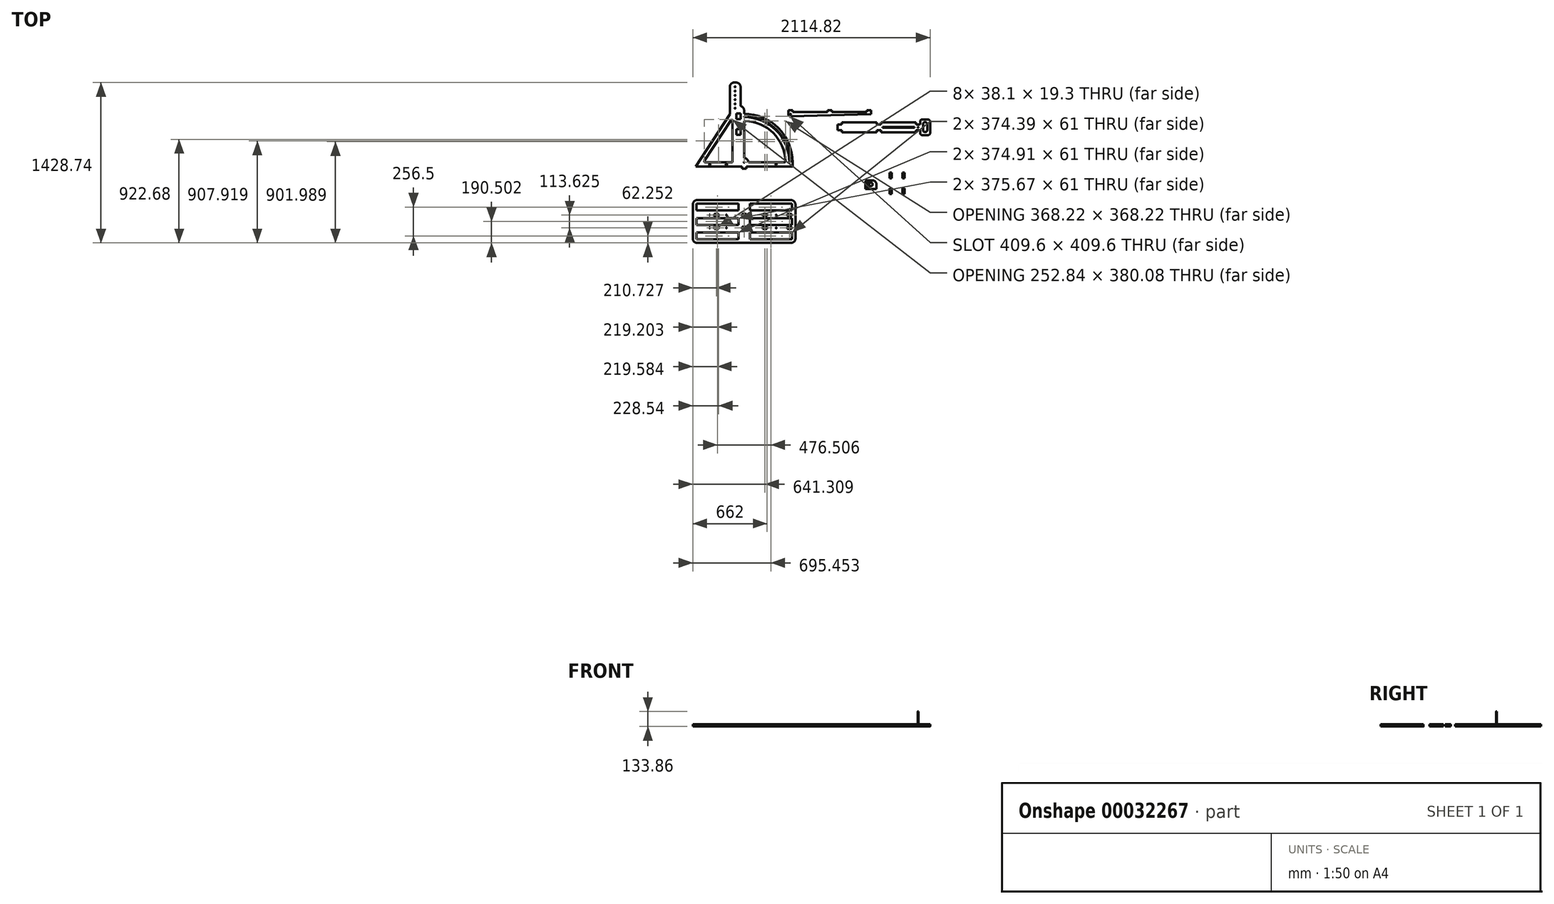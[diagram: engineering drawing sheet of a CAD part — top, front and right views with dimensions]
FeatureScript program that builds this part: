
annotation { "Feature Type Name" : "Feature", "Feature Type Description" : "" }
export const myFeature = defineFeature(function(context is Context, id is Id, definition is map)
    precondition{}
    {
        {
            var Q0;
            Q0=qCreatedBy(makeId("Top.planeOp"),FACE);
            var sketch = newSketch(context, id + "F0", { "sketchPlane" : qUnion([Q0])});
            skLineSegment(sketch, "E0", {"start": v(-431.8, -38.1) * mm, "end": v(431.8, -38.1) * mm});
            skLineSegment(sketch, "E1", {"start": v(0, -38.1) * mm, "end": v(0, 368.3) * mm});
            skPoint(sketch, "E1.startSnap0", {"position": v(0, -38.1) * mm});
            skLineSegment(sketch, "E2", {"start": v(-127, 429.94) * mm, "end": v(-431.8, -38.1) * mm});
            skLineSegment(sketch, "E3", {"start": v(-127, 711.32) * mm, "end": v(-31.75, 710.17) * mm});
            skLineSegment(sketch, "E4", {"start": v(-127, 711.32) * mm, "end": v(-127, 429.94) * mm});
            skLineSegment(sketch, "E5", {"start": v(431.8, -38.1) * mm, "end": v(431.8, 0) * mm});
            skLineSegment(sketch, "E6", {"start": v(409.6, 0) * mm, "end": v(403.2, 0) * mm});
            skArc(sketch, "E7", {"start": v(38.1, 0) * mm, "mid": v(26.94, 26.94) * mm, "end": v(0, 38.1) * mm});
            skLineSegment(sketch, "E8", {"start": v(1130.5, 427.69) * mm, "end": v(1130.5, 446.74) * mm});
            skLineSegment(sketch, "E9", {"start": v(413.41, 409.73) * mm, "end": v(1130.5, 427.69) * mm});
            skPoint(sketch, "E10", {"position": v(412.93, 428.78) * mm});
            skCircle(sketch, "E11", {"center": v(412.93, 428.78) * mm, "radius": 3.37 * mm});
            skArc(sketch, "E12", {"start": v(431.8, 0) * mm, "mid": v(305.33, 305.33) * mm, "end": v(0, 431.8) * mm});
            skArc(sketch, "E13", {"start": v(368.3, 0) * mm, "mid": v(260.43, 260.43) * mm, "end": v(0, 368.3) * mm});
            skArc(sketch, "E14.trimOffspring", {"start": v(403.2, 0) * mm, "mid": v(285.1, 285.1) * mm, "end": v(0, 403.2) * mm});
            skArc(sketch, "E15.trimOffspring", {"start": v(409.6, 0) * mm, "mid": v(289.63, 289.63) * mm, "end": v(0, 409.6) * mm});
            skLineSegment(sketch, "E16", {"start": v(-102.24, 0) * mm, "end": v(-361.52, 0) * mm});
            skLineSegment(sketch, "E17", {"start": v(-361.52, 0) * mm, "end": v(-102.24, 398.13) * mm});
            skLineSegment(sketch, "E18", {"start": v(-102.24, 398.13) * mm, "end": v(-102.24, 0) * mm});
            skLineSegment(sketch, "E19.trimOffspring", {"start": v(368.3, 0) * mm, "end": v(0, 0) * mm});
            skLineSegment(sketch, "E20.trimOffspring", {"start": v(0, 431.8) * mm, "end": v(0, 501.49) * mm});
            skLineSegment(sketch, "E21.trimOffspring", {"start": v(0, 403.2) * mm, "end": v(0, 409.6) * mm});
            skLineSegment(sketch, "E22.rect.bottom", {"start": v(19.05, -38.1) * mm, "end": v(-19.05, -38.1) * mm});
            skLineSegment(sketch, "E22.rect.top", {"start": v(19.05, -56.13) * mm, "end": v(-19.05, -56.13) * mm});
            skLineSegment(sketch, "E22.rect.left", {"start": v(19.05, -38.1) * mm, "end": v(19.05, -56.13) * mm});
            skLineSegment(sketch, "E22.rect.right", {"start": v(-19.05, -38.1) * mm, "end": v(-19.05, -56.13) * mm});
            skLineSegment(sketch, "E23.rect.bottom", {"start": v(-227.42, -38.1) * mm, "end": v(-265.52, -38.1) * mm});
            skLineSegment(sketch, "E23.rect.left", {"start": v(-227.42, -38.1) * mm, "end": v(-227.42, -56.13) * mm});
            skLineSegment(sketch, "E23.rect.top", {"start": v(-227.42, -56.13) * mm, "end": v(-265.52, -56.13) * mm});
            skLineSegment(sketch, "E23.rect.right", {"start": v(-265.52, -38.1) * mm, "end": v(-265.52, -56.13) * mm});
            skLineSegment(sketch, "E24.rect.bottom", {"start": v(422.25, -38.1) * mm, "end": v(384.15, -38.1) * mm});
            skLineSegment(sketch, "E24.rect.left", {"start": v(422.25, -38.1) * mm, "end": v(422.25, -56.13) * mm});
            skLineSegment(sketch, "E24.rect.top", {"start": v(422.25, -56.13) * mm, "end": v(384.15, -56.13) * mm});
            skLineSegment(sketch, "E24.rect.right", {"start": v(384.15, -38.1) * mm, "end": v(384.15, -56.13) * mm});
            skLineSegment(sketch, "E25.rect.bottom", {"start": v(203.2, -38.1) * mm, "end": v(165.1, -38.1) * mm});
            skLineSegment(sketch, "E25.rect.left", {"start": v(203.2, -38.1) * mm, "end": v(203.2, -56.13) * mm});
            skLineSegment(sketch, "E25.rect.top", {"start": v(203.2, -56.13) * mm, "end": v(165.1, -56.13) * mm});
            skLineSegment(sketch, "E25.rect.right", {"start": v(165.1, -38.1) * mm, "end": v(165.1, -56.13) * mm});
            skPoint(sketch, "E26", {"position": v(285.75, -19.05) * mm});
            skCircle(sketch, "E27", {"center": v(-306.23, -19.05) * mm, "radius": 5.33 * mm});
            skCircle(sketch, "E28", {"center": v(-157.54, -19.05) * mm, "radius": 5.33 * mm});
            skCircle(sketch, "E29", {"center": v(285.75, -19.05) * mm, "radius": 5.33 * mm});
            skLineSegment(sketch, "E30", {"start": v(-31.75, 571.18) * mm, "end": v(-31.75, 501.49) * mm});
            skLineSegment(sketch, "E31", {"start": v(-31.75, 501.49) * mm, "end": v(0, 501.49) * mm});
            skLineSegment(sketch, "E32", {"start": v(-31.75, 501.49) * mm, "end": v(-31.75, 710.17) * mm});
            skLineSegment(sketch, "E33", {"start": v(-79.37, 710.75) * mm, "end": v(-79.83, 672.65) * mm});
            skCircle(sketch, "E34", {"center": v(-79.83, 672.65) * mm, "radius": 3.3 * mm});
            skLineSegment(sketch, "E35", {"start": v(-79.83, 672.65) * mm, "end": v(-79.83, 634.55) * mm});
            skCircle(sketch, "E36.0.1.0", {"center": v(-79.83, 634.55) * mm, "radius": 3.3 * mm});
            skCircle(sketch, "E36.0.2.0", {"center": v(-79.83, 596.45) * mm, "radius": 3.3 * mm});
            skCircle(sketch, "E36.0.3.0", {"center": v(-79.83, 558.35) * mm, "radius": 3.3 * mm});
            skLineSegment(sketch, "E36.direction1", {"start": v(-79.83, 672.65) * mm, "end": v(-54.43, 672.65) * mm, "construction": true});
            skLineSegment(sketch, "E36.direction2", {"start": v(-79.83, 672.65) * mm, "end": v(-79.83, 634.55) * mm, "construction": true});
            skCircle(sketch, "E37", {"center": v(0, 0) * mm, "radius": 3.3 * mm});
            skLineSegment(sketch, "E38", {"start": v(393.9, 427.69) * mm, "end": v(393.9, 446.74) * mm});
            skArc(sketch, "E39.trimOffspring", {"start": v(393.9, 427.69) * mm, "mid": v(400.02, 414.76) * mm, "end": v(413.41, 409.73) * mm});
            skLineSegment(sketch, "E40.bottom", {"start": v(832.12, 356.64) * mm, "end": v(1568.72, 356.64) * mm});
            skLineSegment(sketch, "E40.top", {"start": v(832.12, 267.74) * mm, "end": v(1568.72, 267.74) * mm});
            skLineSegment(sketch, "E40.left", {"start": v(832.12, 356.64) * mm, "end": v(832.12, 267.74) * mm});
            skLineSegment(sketch, "E41.bottom", {"start": v(1568.72, 382.04) * mm, "end": v(1657.62, 382.04) * mm});
            skLineSegment(sketch, "E41.top", {"start": v(1568.72, 242.34) * mm, "end": v(1657.62, 242.34) * mm});
            skLineSegment(sketch, "E41.left", {"start": v(1568.72, 382.04) * mm, "end": v(1568.72, 356.64) * mm});
            skLineSegment(sketch, "E41.right", {"start": v(1657.62, 382.04) * mm, "end": v(1657.62, 242.34) * mm});
            skPoint(sketch, "E42", {"position": v(1568.72, 312.19) * mm});
            skLineSegment(sketch, "E43.bottom", {"start": v(1594.12, 357.9) * mm, "end": v(1632.22, 357.9) * mm});
            skLineSegment(sketch, "E43.top", {"start": v(1594.12, 269) * mm, "end": v(1632.22, 269) * mm});
            skLineSegment(sketch, "E43.left", {"start": v(1594.12, 357.9) * mm, "end": v(1594.12, 269) * mm});
            skLineSegment(sketch, "E43.right", {"start": v(1632.22, 357.9) * mm, "end": v(1632.22, 269) * mm});
            skPoint(sketch, "E44", {"position": v(1621.35, 313.44) * mm});
            skLineSegment(sketch, "E45.trimOffspring", {"start": v(1568.72, 267.74) * mm, "end": v(1568.72, 242.34) * mm});
            skLineSegment(sketch, "E46.rect.bottom", {"start": v(432, 464.77) * mm, "end": v(393.9, 464.77) * mm});
            skLineSegment(sketch, "E46.rect.left", {"start": v(432, 464.77) * mm, "end": v(432, 446.74) * mm});
            skLineSegment(sketch, "E46.rect.right", {"start": v(393.9, 464.77) * mm, "end": v(393.9, 446.74) * mm});
            skLineSegment(sketch, "E47.rect.bottom", {"start": v(1130.5, 464.77) * mm, "end": v(1092.4, 464.77) * mm});
            skLineSegment(sketch, "E47.rect.left", {"start": v(1130.5, 464.77) * mm, "end": v(1130.5, 446.74) * mm});
            skLineSegment(sketch, "E47.rect.top", {"start": v(1130.5, 446.74) * mm, "end": v(1092.4, 446.74) * mm});
            skLineSegment(sketch, "E47.rect.right", {"start": v(1092.4, 464.77) * mm, "end": v(1092.4, 446.74) * mm});
            skLineSegment(sketch, "E48.rect.bottom", {"start": v(781.26, 464.77) * mm, "end": v(743.16, 464.77) * mm});
            skLineSegment(sketch, "E48.rect.left", {"start": v(781.26, 464.77) * mm, "end": v(781.26, 446.74) * mm});
            skLineSegment(sketch, "E48.rect.top", {"start": v(781.26, 446.74) * mm, "end": v(743.16, 446.74) * mm});
            skLineSegment(sketch, "E48.rect.right", {"start": v(743.16, 464.77) * mm, "end": v(743.16, 446.74) * mm});
            skPoint(sketch, "E49", {"position": v(762.2, 446.74) * mm});
            skLineSegment(sketch, "E50", {"start": v(393.9, 446.74) * mm, "end": v(1130.5, 446.74) * mm});
            skLineSegment(sketch, "E51.rect.top", {"start": v(870.22, 267.74) * mm, "end": v(832.12, 267.74) * mm});
            skLineSegment(sketch, "E51.rect.left", {"start": v(870.22, 287.04) * mm, "end": v(870.22, 267.74) * mm});
            skLineSegment(sketch, "E51.rect.bottom", {"start": v(870.22, 287.04) * mm, "end": v(832.12, 287.04) * mm});
            skLineSegment(sketch, "E52", {"start": v(832.12, 287.04) * mm, "end": v(832.12, 267.74) * mm});
            skLineSegment(sketch, "E53.rect.top", {"start": v(870.22, 337.34) * mm, "end": v(832.12, 337.34) * mm});
            skLineSegment(sketch, "E53.rect.left", {"start": v(870.22, 356.64) * mm, "end": v(870.22, 337.34) * mm});
            skLineSegment(sketch, "E53.rect.bottom", {"start": v(870.22, 356.64) * mm, "end": v(832.12, 356.64) * mm});
            skLineSegment(sketch, "E54.rect.top", {"start": v(1219.47, 337.34) * mm, "end": v(1181.37, 337.34) * mm});
            skLineSegment(sketch, "E54.rect.left", {"start": v(1219.47, 356.64) * mm, "end": v(1219.47, 337.34) * mm});
            skLineSegment(sketch, "E54.rect.bottom", {"start": v(1219.47, 356.64) * mm, "end": v(1181.37, 356.64) * mm});
            skLineSegment(sketch, "E54.rect.right", {"start": v(1181.37, 356.64) * mm, "end": v(1181.37, 337.34) * mm});
            skLineSegment(sketch, "E55.rect.top", {"start": v(1568.72, 337.34) * mm, "end": v(1530.62, 337.34) * mm});
            skLineSegment(sketch, "E55.rect.left", {"start": v(1568.72, 356.64) * mm, "end": v(1568.72, 337.34) * mm});
            skLineSegment(sketch, "E55.rect.bottom", {"start": v(1568.72, 356.64) * mm, "end": v(1530.62, 356.64) * mm});
            skLineSegment(sketch, "E55.rect.right", {"start": v(1530.62, 356.64) * mm, "end": v(1530.62, 337.34) * mm});
            skLineSegment(sketch, "E56", {"start": v(832.12, 356.64) * mm, "end": v(832.12, 337.34) * mm});
            skPoint(sketch, "E57", {"position": v(1200.42, 356.64) * mm});
            skLineSegment(sketch, "E58.rect.right", {"start": v(1181.37, 287.04) * mm, "end": v(1181.37, 267.74) * mm});
            skLineSegment(sketch, "E58.rect.left", {"start": v(1219.47, 287.04) * mm, "end": v(1219.47, 267.74) * mm});
            skLineSegment(sketch, "E58.rect.top", {"start": v(1219.47, 267.74) * mm, "end": v(1181.37, 267.74) * mm});
            skLineSegment(sketch, "E58.rect.bottom", {"start": v(1219.47, 287.04) * mm, "end": v(1181.37, 287.04) * mm});
            skLineSegment(sketch, "E59.rect.bottom", {"start": v(1568.72, 287.04) * mm, "end": v(1530.62, 287.04) * mm});
            skLineSegment(sketch, "E59.rect.left", {"start": v(1568.72, 287.04) * mm, "end": v(1568.72, 267.74) * mm});
            skLineSegment(sketch, "E59.rect.right", {"start": v(1530.62, 287.04) * mm, "end": v(1530.62, 267.74) * mm});
            skLineSegment(sketch, "E59.rect.top", {"start": v(1568.72, 267.74) * mm, "end": v(1530.62, 267.74) * mm});
            skPoint(sketch, "E60", {"position": v(1613.17, 357.9) * mm});
            skPoint(sketch, "E61", {"position": v(1200.42, 267.74) * mm});
            skLineSegment(sketch, "E62.bottom", {"start": v(-457.2, -336.88) * mm, "end": v(457.2, -336.88) * mm});
            skLineSegment(sketch, "E62.top", {"start": v(-457.2, -717.88) * mm, "end": v(457.2, -717.88) * mm});
            skLineSegment(sketch, "E62.left", {"start": v(-457.2, -336.88) * mm, "end": v(-457.2, -717.88) * mm});
            skLineSegment(sketch, "E62.right", {"start": v(457.2, -336.88) * mm, "end": v(457.2, -717.88) * mm});
            skLineSegment(sketch, "E63.left", {"start": v(-457.2, -479.75) * mm, "end": v(-457.2, -575) * mm});
            skLineSegment(sketch, "E63.right", {"start": v(457.2, -479.75) * mm, "end": v(457.2, -575) * mm});
            skPoint(sketch, "E64", {"position": v(-457.2, -527.38) * mm});
            skLineSegment(sketch, "E65.rect.left", {"start": v(-227.42, -461.38) * mm, "end": v(-227.42, -480.68) * mm});
            skLineSegment(sketch, "E65.rect.top", {"start": v(-227.42, -480.68) * mm, "end": v(-265.52, -480.68) * mm});
            skLineSegment(sketch, "E66", {"start": v(-265.52, -461.38) * mm, "end": v(-265.52, -480.68) * mm});
            skLineSegment(sketch, "E65.rect.bottom", {"start": v(-227.42, -461.38) * mm, "end": v(-265.52, -461.38) * mm});
            skLineSegment(sketch, "E67.rect.left", {"start": v(19.05, -460.45) * mm, "end": v(19.05, -479.75) * mm});
            skLineSegment(sketch, "E67.rect.top", {"start": v(19.05, -479.75) * mm, "end": v(-19.05, -479.75) * mm});
            skLineSegment(sketch, "E68", {"start": v(-19.05, -460.45) * mm, "end": v(-19.05, -479.75) * mm});
            skLineSegment(sketch, "E67.rect.bottom", {"start": v(19.05, -460.45) * mm, "end": v(-19.05, -460.45) * mm});
            skLineSegment(sketch, "E69.rect.left", {"start": v(203.2, -460.45) * mm, "end": v(203.2, -479.75) * mm});
            skLineSegment(sketch, "E69.rect.top", {"start": v(203.2, -479.75) * mm, "end": v(165.1, -479.75) * mm});
            skLineSegment(sketch, "E70", {"start": v(165.1, -460.45) * mm, "end": v(165.1, -479.75) * mm});
            skLineSegment(sketch, "E69.rect.bottom", {"start": v(203.2, -460.45) * mm, "end": v(165.1, -460.45) * mm});
            skLineSegment(sketch, "E71.rect.left", {"start": v(422.25, -460.45) * mm, "end": v(422.25, -479.75) * mm});
            skLineSegment(sketch, "E71.rect.top", {"start": v(422.25, -479.75) * mm, "end": v(384.15, -479.75) * mm});
            skLineSegment(sketch, "E72", {"start": v(384.15, -460.45) * mm, "end": v(384.15, -479.75) * mm});
            skLineSegment(sketch, "E71.rect.bottom", {"start": v(422.25, -460.45) * mm, "end": v(384.15, -460.45) * mm});
            skLineSegment(sketch, "E73.rect.left", {"start": v(-227.42, -575) * mm, "end": v(-227.42, -594.3) * mm});
            skLineSegment(sketch, "E73.rect.top", {"start": v(-227.42, -594.3) * mm, "end": v(-265.52, -594.3) * mm});
            skLineSegment(sketch, "E74", {"start": v(-265.52, -575) * mm, "end": v(-265.52, -594.3) * mm});
            skLineSegment(sketch, "E73.rect.bottom", {"start": v(-227.42, -575) * mm, "end": v(-265.52, -575) * mm});
            skLineSegment(sketch, "E75.rect.left", {"start": v(19.05, -575) * mm, "end": v(19.05, -594.3) * mm});
            skLineSegment(sketch, "E75.rect.top", {"start": v(19.05, -594.3) * mm, "end": v(-19.05, -594.3) * mm});
            skLineSegment(sketch, "E76", {"start": v(-19.05, -575) * mm, "end": v(-19.05, -594.3) * mm});
            skLineSegment(sketch, "E75.rect.bottom", {"start": v(19.05, -575) * mm, "end": v(-19.05, -575) * mm});
            skLineSegment(sketch, "E77.rect.left", {"start": v(203.2, -575) * mm, "end": v(203.2, -594.3) * mm});
            skLineSegment(sketch, "E77.rect.top", {"start": v(203.2, -594.3) * mm, "end": v(165.1, -594.3) * mm});
            skLineSegment(sketch, "E78", {"start": v(165.1, -575) * mm, "end": v(165.1, -594.3) * mm});
            skLineSegment(sketch, "E77.rect.bottom", {"start": v(203.2, -575) * mm, "end": v(165.1, -575) * mm});
            skLineSegment(sketch, "E79.rect.left", {"start": v(422.25, -575) * mm, "end": v(422.25, -594.3) * mm});
            skLineSegment(sketch, "E79.rect.top", {"start": v(422.25, -594.3) * mm, "end": v(384.15, -594.3) * mm});
            skLineSegment(sketch, "E80", {"start": v(384.15, -575) * mm, "end": v(384.15, -594.3) * mm});
            skLineSegment(sketch, "E79.rect.bottom", {"start": v(422.25, -575) * mm, "end": v(384.15, -575) * mm});
            skLineSegment(sketch, "E81", {"start": v(-265.52, -38.1) * mm, "end": v(-265.52, -32.4) * mm, "construction": true});
            skPoint(sketch, "E82", {"position": v(-265.52, -38.1) * mm});
            skPoint(sketch, "E83.startSnap0", {"position": v(-265.52, -471.03) * mm});
            skPoint(sketch, "E83.endSnap0", {"position": v(203.2, -470.1) * mm});
            skPoint(sketch, "E84.endSnap0", {"position": v(203.2, -584.66) * mm});
            skCircle(sketch, "E85", {"center": v(-306.23, -470.12) * mm, "radius": 3.3 * mm});
            skCircle(sketch, "E86", {"center": v(-306.23, -584.66) * mm, "radius": 3.3 * mm});
            skCircle(sketch, "E87", {"center": v(-157.54, -470.1) * mm, "radius": 3.3 * mm});
            skCircle(sketch, "E88", {"center": v(-157.54, -584.66) * mm, "radius": 3.3 * mm});
            skCircle(sketch, "E89", {"center": v(285.75, -470.1) * mm, "radius": 3.3 * mm});
            skCircle(sketch, "E90", {"center": v(285.75, -584.66) * mm, "radius": 3.3 * mm});
            skCircle(sketch, "E91", {"center": v(1549.67, 312.19) * mm, "radius": 3.3 * mm});
            skLineSegment(sketch, "E92", {"start": v(-31.75, 436.83) * mm, "end": v(-31.75, 386.03) * mm});
            skLineSegment(sketch, "E93", {"start": v(-31.75, 386.03) * mm, "end": v(-69.34, 386.03) * mm});
            skLineSegment(sketch, "E94", {"start": v(-69.34, 386.03) * mm, "end": v(-69.34, 436.83) * mm});
            skLineSegment(sketch, "E95", {"start": v(-69.34, 436.83) * mm, "end": v(-31.75, 436.83) * mm});
            skLineSegment(sketch, "E96", {"start": v(-31.75, 297.13) * mm, "end": v(-31.75, 246.33) * mm});
            skLineSegment(sketch, "E97", {"start": v(-69.34, 246.33) * mm, "end": v(-69.34, 297.13) * mm});
            skLineSegment(sketch, "E98", {"start": v(-31.75, 246.33) * mm, "end": v(-69.34, 246.33) * mm});
            skLineSegment(sketch, "E99", {"start": v(-69.34, 297.13) * mm, "end": v(-31.75, 297.13) * mm});
            skLineSegment(sketch, "E100.bottom", {"start": v(1517.92, 315.5) * mm, "end": v(1232.17, 315.5) * mm});
            skLineSegment(sketch, "E100.top", {"start": v(1517.92, 308.89) * mm, "end": v(1232.17, 308.89) * mm});
            skLineSegment(sketch, "E100.left", {"start": v(1517.92, 315.5) * mm, "end": v(1517.92, 308.89) * mm});
            skLineSegment(sketch, "E100.right", {"start": v(1232.17, 315.5) * mm, "end": v(1232.17, 308.89) * mm});
            skLineSegment(sketch, "E101", {"start": v(1632.22, 312.19) * mm, "end": v(1517.92, 312.19) * mm, "construction": true});
            skPoint(sketch, "E101.startSnap0", {"position": v(1632.22, 313.44) * mm});
            skPoint(sketch, "E102", {"position": v(1517.92, 312.19) * mm});
            skLineSegment(sketch, "E103.bottom", {"start": v(1079.65, -160.08) * mm, "end": v(1179.88, -160.08) * mm});
            skLineSegment(sketch, "E103.top", {"start": v(1079.65, -236.28) * mm, "end": v(1179.88, -236.28) * mm});
            skLineSegment(sketch, "E103.left", {"start": v(1079.65, -160.08) * mm, "end": v(1079.65, -236.28) * mm});
            skLineSegment(sketch, "E103.right", {"start": v(1179.88, -160.08) * mm, "end": v(1179.88, -236.28) * mm});
            skArc(sketch, "E104", {"start": v(1115.7, -189.34) * mm, "mid": v(1138.42, -210) * mm, "end": v(1128.78, -180.84) * mm});
            skPoint(sketch, "E104.centerSnap0", {"position": v(1129.77, -236.28) * mm});
            skLineSegment(sketch, "E105", {"start": v(1079.65, -183.9) * mm, "end": v(1128.78, -180.84) * mm});
            skLineSegment(sketch, "E106", {"start": v(1115.7, -189.34) * mm, "end": v(1079.65, -191.59) * mm});
            skLineSegment(sketch, "E107.bottom", {"start": v(1297.48, -92.92) * mm, "end": v(1429.82, -92.92) * mm});
            skLineSegment(sketch, "E107.top", {"start": v(1297.48, -283.42) * mm, "end": v(1429.82, -283.42) * mm});
            skLineSegment(sketch, "E107.left", {"start": v(1297.48, -92.92) * mm, "end": v(1297.48, -143.72) * mm});
            skLineSegment(sketch, "E107.right", {"start": v(1429.82, -92.92) * mm, "end": v(1429.82, -143.72) * mm});
            skLineSegment(sketch, "E108", {"start": v(1297.48, -143.72) * mm, "end": v(1297.48, -92.92) * mm});
            skLineSegment(sketch, "E109", {"start": v(1297.48, -92.92) * mm, "end": v(1315.77, -92.92) * mm});
            skLineSegment(sketch, "E110", {"start": v(1315.77, -143.72) * mm, "end": v(1297.48, -143.72) * mm});
            skLineSegment(sketch, "E111", {"start": v(1315.77, -92.92) * mm, "end": v(1315.77, -143.72) * mm});
            skLineSegment(sketch, "E112", {"start": v(1411.53, -92.92) * mm, "end": v(1429.82, -92.92) * mm});
            skLineSegment(sketch, "E113", {"start": v(1411.53, -143.72) * mm, "end": v(1411.53, -92.92) * mm});
            skLineSegment(sketch, "E114", {"start": v(1429.82, -143.72) * mm, "end": v(1411.53, -143.72) * mm});
            skLineSegment(sketch, "E115", {"start": v(1411.53, -232.62) * mm, "end": v(1429.82, -232.62) * mm});
            skLineSegment(sketch, "E116", {"start": v(1411.53, -283.42) * mm, "end": v(1411.53, -232.62) * mm});
            skLineSegment(sketch, "E117", {"start": v(1429.82, -232.62) * mm, "end": v(1429.82, -283.42) * mm});
            skLineSegment(sketch, "E118", {"start": v(1429.82, -283.42) * mm, "end": v(1411.53, -283.42) * mm});
            skLineSegment(sketch, "E119", {"start": v(1297.48, -232.62) * mm, "end": v(1315.77, -232.62) * mm});
            skLineSegment(sketch, "E120", {"start": v(1297.48, -283.42) * mm, "end": v(1297.48, -232.62) * mm});
            skLineSegment(sketch, "E121", {"start": v(1315.77, -232.62) * mm, "end": v(1315.77, -283.42) * mm});
            skLineSegment(sketch, "E122", {"start": v(1315.77, -283.42) * mm, "end": v(1297.48, -283.42) * mm});
            skLineSegment(sketch, "E123", {"start": v(1315.77, -143.72) * mm, "end": v(1315.77, -232.62) * mm});
            skLineSegment(sketch, "E124", {"start": v(1411.53, -143.72) * mm, "end": v(1411.53, -232.62) * mm});
            skLineSegment(sketch, "E125.trimOffspring", {"start": v(1297.48, -232.62) * mm, "end": v(1297.48, -283.42) * mm});
            skCircle(sketch, "E126", {"center": v(1098.7, -217.23) * mm, "radius": 5.33 * mm});
            skPoint(sketch, "E127", {"position": v(1098.7, -211.9) * mm});
            skLineSegment(sketch, "E128", {"start": v(-50.54, -368.63) * mm, "end": v(-50.54, -429.63) * mm});
            skPoint(sketch, "E128.startSnap0", {"position": v(-50.54, 246.33) * mm});
            skPoint(sketch, "E129.endSnap0", {"position": v(0, -575) * mm});
            skLineSegment(sketch, "E130.MirrorCS", {"start": v(51.06, -368.63) * mm, "end": v(51.06, -429.63) * mm});
            skLineSegment(sketch, "E131.bottom", {"start": v(-50.54, -429.63) * mm, "end": v(-425.45, -429.63) * mm});
            skLineSegment(sketch, "E131.top", {"start": v(-50.54, -368.63) * mm, "end": v(-425.45, -368.63) * mm});
            skLineSegment(sketch, "E131.left", {"start": v(-50.54, -429.63) * mm, "end": v(-50.54, -368.63) * mm});
            skLineSegment(sketch, "E131.right", {"start": v(-425.45, -429.63) * mm, "end": v(-425.45, -368.63) * mm});
            skLineSegment(sketch, "E132.MirrorCS", {"start": v(-50.54, -686.13) * mm, "end": v(-426.21, -686.13) * mm});
            skLineSegment(sketch, "E133.MirrorCS", {"start": v(-50.54, -625.13) * mm, "end": v(-425.45, -625.13) * mm});
            skLineSegment(sketch, "E134.MirrorCS", {"start": v(-425.45, -625.13) * mm, "end": v(-425.45, -686.13) * mm});
            skLineSegment(sketch, "E135.MirrorCS", {"start": v(51.06, -368.63) * mm, "end": v(425.45, -368.63) * mm});
            skLineSegment(sketch, "E136.MirrorCS", {"start": v(425.45, -429.63) * mm, "end": v(425.45, -368.63) * mm});
            skLineSegment(sketch, "E137.MirrorCS", {"start": v(51.06, -429.63) * mm, "end": v(425.45, -429.63) * mm});
            skLineSegment(sketch, "E138.MirrorCS", {"start": v(425.45, -625.13) * mm, "end": v(425.45, -686.13) * mm});
            skLineSegment(sketch, "E139.MirrorCS", {"start": v(51.06, -625.13) * mm, "end": v(425.45, -625.13) * mm});
            skLineSegment(sketch, "E140.MirrorCS", {"start": v(51.06, -686.13) * mm, "end": v(425.45, -686.13) * mm});
            skPoint(sketch, "E141.orphan", {"position": v(-50.54, -336.88) * mm});
            skPoint(sketch, "E142.orphan", {"position": v(51.06, -336.88) * mm});
            skLineSegment(sketch, "E143.trimOffspring", {"start": v(51.06, -625.13) * mm, "end": v(51.06, -686.13) * mm});
            skLineSegment(sketch, "E144.trimOffspring", {"start": v(-50.54, -625.13) * mm, "end": v(-50.54, -686.13) * mm});
            skLineSegment(sketch, "E145", {"start": v(1530.62, 337.34) * mm, "end": v(1568.72, 287.04) * mm, "construction": true});
            skLineSegment(sketch, "E146", {"start": v(1530.62, 287.04) * mm, "end": v(1568.72, 337.34) * mm, "construction": true});
            skLineSegment(sketch, "E147", {"start": v(-49.78, -496.88) * mm, "end": v(-49.78, -557.88) * mm});
            skLineSegment(sketch, "E148.top", {"start": v(-49.78, -496.88) * mm, "end": v(-425.45, -496.88) * mm});
            skLineSegment(sketch, "E148.bottom", {"start": v(-49.78, -557.88) * mm, "end": v(-425.45, -557.88) * mm});
            skLineSegment(sketch, "E148.right", {"start": v(-425.45, -557.88) * mm, "end": v(-425.45, -496.88) * mm});
            skLineSegment(sketch, "E148.left", {"start": v(-49.78, -557.88) * mm, "end": v(-49.78, -496.88) * mm});
            skLineSegment(sketch, "E149", {"start": v(-457.2, -527.38) * mm, "end": v(457.2, -527.38) * mm, "construction": true});
            skLineSegment(sketch, "E150", {"start": v(-425.45, -429.63) * mm, "end": v(-425.45, -625.13) * mm, "construction": true});
            skLineSegment(sketch, "E151", {"start": v(51.06, -429.63) * mm, "end": v(51.06, -625.13) * mm, "construction": true});
            skPoint(sketch, "E152", {"position": v(-425.45, -527.38) * mm});
            skPoint(sketch, "E153", {"position": v(51.06, -527.38) * mm});
            skLineSegment(sketch, "E154.top", {"start": v(426.72, -496.88) * mm, "end": v(51.06, -496.88) * mm});
            skLineSegment(sketch, "E154.bottom", {"start": v(426.72, -557.88) * mm, "end": v(51.06, -557.88) * mm});
            skLineSegment(sketch, "E154.left", {"start": v(426.72, -557.88) * mm, "end": v(426.72, -496.88) * mm});
            skLineSegment(sketch, "E154.right", {"start": v(51.06, -557.88) * mm, "end": v(51.06, -496.88) * mm});
            skLineSegment(sketch, "E155", {"start": v(426.72, -496.88) * mm, "end": v(426.72, -557.88) * mm});
            skCircle(sketch, "E156.0.0.4", {"center": v(-79.83, 520.25) * mm, "radius": 3.3 * mm});
            skCircle(sketch, "E156.0.0.5", {"center": v(-79.83, 482.15) * mm, "radius": 3.3 * mm});
            skLineSegment(sketch, "E157", {"start": v(457.2, -336.88) * mm, "end": v(863.6, -336.88) * mm});
            skLineSegment(sketch, "E158", {"start": v(863.6, -336.88) * mm, "end": v(863.6, -717.88) * mm});
            skLineSegment(sketch, "E159", {"start": v(863.6, -717.88) * mm, "end": v(457.2, -717.88) * mm});
            skLineSegment(sketch, "E160.bottom", {"start": v(488.95, -368.63) * mm, "end": v(812.8, -368.63) * mm});
            skLineSegment(sketch, "E160.top", {"start": v(488.95, -429.63) * mm, "end": v(812.8, -429.63) * mm});
            skLineSegment(sketch, "E160.left", {"start": v(488.95, -368.63) * mm, "end": v(488.95, -429.63) * mm});
            skLineSegment(sketch, "E160.right", {"start": v(812.8, -368.63) * mm, "end": v(812.8, -429.63) * mm});
            skLineSegment(sketch, "E161.bottom", {"start": v(488.95, -496.88) * mm, "end": v(812.8, -496.88) * mm});
            skLineSegment(sketch, "E161.top", {"start": v(488.95, -557.88) * mm, "end": v(812.8, -557.88) * mm});
            skLineSegment(sketch, "E161.left", {"start": v(488.95, -496.88) * mm, "end": v(488.95, -557.88) * mm});
            skLineSegment(sketch, "E161.right", {"start": v(812.8, -496.88) * mm, "end": v(812.8, -557.88) * mm});
            skLineSegment(sketch, "E162.bottom", {"start": v(488.95, -625.13) * mm, "end": v(812.8, -625.13) * mm});
            skLineSegment(sketch, "E162.top", {"start": v(488.95, -686.13) * mm, "end": v(812.8, -686.13) * mm});
            skLineSegment(sketch, "E162.left", {"start": v(488.95, -625.13) * mm, "end": v(488.95, -686.13) * mm});
            skLineSegment(sketch, "E162.right", {"start": v(812.8, -625.13) * mm, "end": v(812.8, -686.13) * mm});
            skCircle(sketch, "E163", {"center": v(838.2, -463.25) * mm, "radius": 3.17 * mm});
            skLineSegment(sketch, "E164", {"start": v(812.8, -429.63) * mm, "end": v(812.8, -496.88) * mm, "construction": true});
            skLineSegment(sketch, "E165", {"start": v(812.8, -496.88) * mm, "end": v(863.6, -496.88) * mm, "construction": true});
            skPoint(sketch, "E166", {"position": v(838.2, -496.88) * mm});
            skPoint(sketch, "E167", {"position": v(812.8, -463.25) * mm});
            skCircle(sketch, "E168.MirrorC", {"center": v(838.2, -591.5) * mm, "radius": 3.17 * mm});
            skSolve(sketch);
        }
        {
            var Q0;
            {var subQ6=sQuery(id+"F0.wireOp",EDGE,"E2");Q0=makeQuery(id+"F0.imprint","IMPRINT",FACE,{"disambiguationData":[TD([[makeQuery(id+"F0.imprint","IMPRINT",EDGE,{"derivedFrom":subQ6}),1.0]])]});}
            var Q1;
            Q1=makeQuery(id+"F0.imprint","IMPRINT",FACE,{"disambiguationData":[TD([[makeQuery(id+"F0.imprint","IMPRINT",EDGE,{"derivedFrom":sQuery(id+"F0.wireOp",EDGE,"E23.rect.bottom")}),1.0]])]});
            var Q2;
            Q2=makeQuery(id+"F0.imprint","IMPRINT",FACE,{"disambiguationData":[TD([[makeQuery(id+"F0.imprint","IMPRINT",EDGE,{"derivedFrom":sQuery(id+"F0.wireOp",EDGE,"E22.rect.top")}),-1.0]])]});
            var Q3;
            Q3=makeQuery(id+"F0.imprint","IMPRINT",FACE,{"disambiguationData":[TD([[makeQuery(id+"F0.imprint","IMPRINT",EDGE,{"derivedFrom":sQuery(id+"F0.wireOp",EDGE,"E24.rect.bottom")}),1.0]])]});
            var Q4;
            Q4=makeQuery(id+"F0.imprint","IMPRINT",FACE,{"disambiguationData":[TD([[makeQuery(id+"F0.imprint","IMPRINT",EDGE,{"derivedFrom":sQuery(id+"F0.wireOp",EDGE,"E25.rect.bottom")}),1.0]])]});
            var Q5;
            {var subQ3=sQuery(id+"F0.wireOp",EDGE,"E7");Q5=makeQuery(id+"F0.imprint","IMPRINT",FACE,{"disambiguationData":[TD([[makeQuery(id+"F0.imprint","IMPRINT",EDGE,{"derivedFrom":subQ3}),1.0]])]});}
            var Q6;
            Q6=makeQuery(id+"F0.imprint","IMPRINT",FACE,{"disambiguationData":[TD([[makeQuery(id+"F0.imprint","IMPRINT",EDGE,{"derivedFrom":sQuery(id+"F0.wireOp",EDGE,"E8")}),1.0]])]});
            var Q7;
            Q7=makeQuery(id+"F0.imprint","IMPRINT",FACE,{"disambiguationData":[TD([[makeQuery(id+"F0.imprint","IMPRINT",EDGE,{"derivedFrom":sQuery(id+"F0.wireOp",EDGE,"E40.bottom")}),-1.0]])]});
            var Q8;
            Q8=makeQuery(id+"F0.imprint","IMPRINT",FACE,{"disambiguationData":[TD([[makeQuery(id+"F0.imprint","IMPRINT",EDGE,{"derivedFrom":sQuery(id+"F0.wireOp",EDGE,"E48.rect.bottom")}),1.0]])]});
            var Q9;
            Q9=makeQuery(id+"F0.imprint","IMPRINT",FACE,{"disambiguationData":[TD([[makeQuery(id+"F0.imprint","IMPRINT",EDGE,{"derivedFrom":sQuery(id+"F0.wireOp",EDGE,"E47.rect.bottom")}),1.0]])]});
            var Q10;
            Q10=makeQuery(id+"F0.imprint","IMPRINT",FACE,{"disambiguationData":[TD([[makeQuery(id+"F0.imprint","IMPRINT",EDGE,{"derivedFrom":sQuery(id+"F0.wireOp",EDGE,"E46.rect.bottom")}),1.0]])]});
            var Q11;
            {var subQ0=sQuery(id+"F0.wireOp",EDGE,"E62.bottom");Q11=makeQuery(id+"F0.imprint","IMPRINT",FACE,{"disambiguationData":[TD([[makeQuery(id+"F0.imprint","IMPRINT",EDGE,{"derivedFrom":subQ0}),-1.0]])]});}
            var Q12;
            {var subQ4=sQuery(id+"F0.wireOp",EDGE,"E103.bottom");Q12=makeQuery(id+"F0.imprint","IMPRINT",FACE,{"disambiguationData":[TD([[makeQuery(id+"F0.imprint","IMPRINT",EDGE,{"derivedFrom":subQ4}),-1.0]])]});}
            var Q13;
            Q13=makeQuery(id+"F0.imprint","IMPRINT",FACE,{"disambiguationData":[TD([[makeQuery(id+"F0.imprint","IMPRINT",EDGE,{"derivedFrom":sQuery(id+"F0.wireOp",EDGE,"E107.bottom")}),-1.0]])]});
            var Q14;
            Q14=makeQuery(id+"F0.imprint","IMPRINT",FACE,{"disambiguationData":[TD([[makeQuery(id+"F0.imprint","IMPRINT",EDGE,{"derivedFrom":sQuery(id+"F0.wireOp",EDGE,"E108")}),-1.0]])]});
            var Q15;
            Q15=makeQuery(id+"F0.imprint","IMPRINT",FACE,{"disambiguationData":[TD([[makeQuery(id+"F0.imprint","IMPRINT",EDGE,{"derivedFrom":sQuery(id+"F0.wireOp",EDGE,"E112")}),-1.0]])]});
            var Q16;
            Q16=makeQuery(id+"F0.imprint","IMPRINT",FACE,{"disambiguationData":[TD([[makeQuery(id+"F0.imprint","IMPRINT",EDGE,{"derivedFrom":sQuery(id+"F0.wireOp",EDGE,"E119")}),-1.0]])]});
            var Q17;
            Q17=makeQuery(id+"F0.imprint","IMPRINT",FACE,{"disambiguationData":[TD([[makeQuery(id+"F0.imprint","IMPRINT",EDGE,{"derivedFrom":sQuery(id+"F0.wireOp",EDGE,"E115")}),-1.0]])]});
            var Q18;
            {var subQ2=sQuery(id+"F0.wireOp",EDGE,"E63.right");Q18=makeQuery(id+"F0.imprint","IMPRINT",FACE,{"disambiguationData":[TD([[makeQuery(id+"F0.imprint","IMPRINT",EDGE,{"derivedFrom":subQ2}),1.0]])]});}
            extrude(context, id + "F1", {"entities" : qUnion([Q0, Q1, Q2, Q3, Q4, Q5, Q6, Q7, Q8, Q9, Q10, Q11, Q12, Q13, Q14, Q15, Q16, Q17, Q18]), "depth" : 18.8 * mm});
        }
        {
            var Q0;
            Q0=makeQuery(id+"F1.opExtrude","SWEPT_EDGE",EDGE,{"disambiguationData":[OSD([sQuery(id+"F0.wireOp",EDGE,"E3"),sQuery(id+"F0.wireOp",EDGE,"E32")])]});
            var Q1;
            Q1=makeQuery(id+"F1.opExtrude","SWEPT_EDGE",EDGE,{"disambiguationData":[OSD([sQuery(id+"F0.wireOp",EDGE,"E3"),sQuery(id+"F0.wireOp",EDGE,"E4")])]});
            var Q2;
            Q2=makeQuery(id+"F1.opExtrude","SWEPT_EDGE",EDGE,{"disambiguationData":[OSD([sQuery(id+"F0.wireOp",EDGE,"E20.trimOffspring"),sQuery(id+"F0.wireOp",EDGE,"E31")])]});
            var Q3;
            Q3=makeQuery(id+"F1.opExtrude","SWEPT_EDGE",EDGE,{"disambiguationData":[OSD([sQuery(id+"F0.wireOp",EDGE,"E62.top"),sQuery(id+"F0.wireOp",EDGE,"E62.left")])]});
            var Q4;
            Q4=makeQuery(id+"F1.opExtrude","SWEPT_EDGE",EDGE,{"disambiguationData":[OSD([sQuery(id+"F0.wireOp",EDGE,"E62.bottom"),sQuery(id+"F0.wireOp",EDGE,"E62.left")])]});
            var Q5;
            Q5=makeQuery(id+"F1.opExtrude","SWEPT_EDGE",EDGE,{"disambiguationData":[OSD([sQuery(id+"F0.wireOp",EDGE,"E103.bottom"),sQuery(id+"F0.wireOp",EDGE,"E103.right")])]});
            var Q6;
            Q6=makeQuery(id+"F1.opExtrude","SWEPT_EDGE",EDGE,{"disambiguationData":[OSD([sQuery(id+"F0.wireOp",EDGE,"E158"),sQuery(id+"F0.wireOp",EDGE,"E159")])]});
            var Q7;
            Q7=makeQuery(id+"F1.opExtrude","SWEPT_EDGE",EDGE,{"disambiguationData":[OSD([sQuery(id+"F0.wireOp",EDGE,"E157"),sQuery(id+"F0.wireOp",EDGE,"E158")])]});
            fillet(context, id + "F2", {"entities" : qUnion([Q0, Q1, Q2, Q3, Q4, Q5, Q6, Q7]), "radius" : 38.1 * mm, "tangentPropagation" : true, "allowEdgeOverflow" : false});
        }
        {
            var Q0;
            Q0=makeQuery(id+"F1.opExtrude","SWEPT_EDGE",EDGE,{"disambiguationData":[OSD([sQuery(id+"F0.wireOp",EDGE,"E17"),sQuery(id+"F0.wireOp",EDGE,"E18")])]});
            var Q1;
            Q1=makeQuery(id+"F1.opExtrude","SWEPT_EDGE",EDGE,{"disambiguationData":[OSD([sQuery(id+"F0.wireOp",EDGE,"E1"),sQuery(id+"F0.wireOp",EDGE,"E13")])]});
            var Q2;
            Q2=makeQuery(id+"F1.opExtrude","SWEPT_EDGE",EDGE,{"disambiguationData":[OSD([sQuery(id+"F0.wireOp",EDGE,"E16"),sQuery(id+"F0.wireOp",EDGE,"E17")])]});
            var Q3;
            Q3=makeQuery(id+"F1.opExtrude","SWEPT_EDGE",EDGE,{"disambiguationData":[OSD([sQuery(id+"F0.wireOp",EDGE,"E16"),sQuery(id+"F0.wireOp",EDGE,"E18")])]});
            var Q4;
            Q4=makeQuery(id+"F1.opExtrude","SWEPT_EDGE",EDGE,{"disambiguationData":[OSD([sQuery(id+"F0.wireOp",EDGE,"E1"),sQuery(id+"F0.wireOp",EDGE,"E7")])]});
            var Q5;
            Q5=makeQuery(id+"F1.opExtrude","SWEPT_EDGE",EDGE,{"disambiguationData":[OSD([sQuery(id+"F0.wireOp",EDGE,"E7"),sQuery(id+"F0.wireOp",EDGE,"E19.trimOffspring")])]});
            var Q6;
            Q6=makeQuery(id+"F1.opExtrude","SWEPT_EDGE",EDGE,{"disambiguationData":[OSD([sQuery(id+"F0.wireOp",EDGE,"E13"),sQuery(id+"F0.wireOp",EDGE,"E19.trimOffspring")])]});
            var Q7;
            Q7=makeQuery(id+"F2.opFillet","BLEND_EDGE",EDGE,{"blendedFrom":[makeQuery(id+"F1.opExtrude","SWEPT_EDGE",EDGE,{"disambiguationData":[OSD([sQuery(id+"F0.wireOp",EDGE,"E20.trimOffspring"),sQuery(id+"F0.wireOp",EDGE,"E31")])]}),makeQuery(id+"F1.opExtrude","SWEPT_FACE",FACE,{"disambiguationData":[OSD([sQuery(id+"F0.wireOp",EDGE,"E32")])]})],"blendedInto":[makeQuery(id+"F1.opExtrude","SWEPT_FACE",FACE,{"disambiguationData":[OSD([sQuery(id+"F0.wireOp",EDGE,"E32")])]})]});
            fillet(context, id + "F3", {"entities" : qUnion([Q0, Q1, Q2, Q3, Q4, Q5, Q6, Q7]), "radius" : 7.62 * mm, "tangentPropagation" : true, "allowEdgeOverflow" : false});
        }
        {
            var Q0;
            Q0=makeQuery(id+"F1.opExtrude","SWEPT_EDGE",EDGE,{"disambiguationData":[OSD([sQuery(id+"F0.wireOp",EDGE,"E43.top"),sQuery(id+"F0.wireOp",EDGE,"E43.left")])]});
            var Q1;
            Q1=makeQuery(id+"F1.opExtrude","SWEPT_EDGE",EDGE,{"disambiguationData":[OSD([sQuery(id+"F0.wireOp",EDGE,"E41.top"),sQuery(id+"F0.wireOp",EDGE,"E41.right")])]});
            var Q2;
            Q2=makeQuery(id+"F1.opExtrude","SWEPT_EDGE",EDGE,{"disambiguationData":[OSD([sQuery(id+"F0.wireOp",EDGE,"E41.bottom"),sQuery(id+"F0.wireOp",EDGE,"E41.right")])]});
            var Q3;
            Q3=makeQuery(id+"F1.opExtrude","SWEPT_EDGE",EDGE,{"disambiguationData":[OSD([sQuery(id+"F0.wireOp",EDGE,"E41.bottom"),sQuery(id+"F0.wireOp",EDGE,"E41.left")])]});
            var Q4;
            Q4=makeQuery(id+"F1.opExtrude","SWEPT_EDGE",EDGE,{"disambiguationData":[OSD([sQuery(id+"F0.wireOp",EDGE,"E41.top"),sQuery(id+"F0.wireOp",EDGE,"E45.trimOffspring")])]});
            var Q5;
            Q5=makeQuery(id+"F1.opExtrude","SWEPT_EDGE",EDGE,{"disambiguationData":[OSD([sQuery(id+"F0.wireOp",EDGE,"E43.bottom"),sQuery(id+"F0.wireOp",EDGE,"E43.left")])]});
            var Q6;
            Q6=makeQuery(id+"F1.opExtrude","SWEPT_EDGE",EDGE,{"disambiguationData":[OSD([sQuery(id+"F0.wireOp",EDGE,"E43.bottom"),sQuery(id+"F0.wireOp",EDGE,"E43.right")])]});
            var Q7;
            Q7=makeQuery(id+"F1.opExtrude","SWEPT_EDGE",EDGE,{"disambiguationData":[OSD([sQuery(id+"F0.wireOp",EDGE,"E43.top"),sQuery(id+"F0.wireOp",EDGE,"E43.right")])]});
            var Q8;
            Q8=makeQuery(id+"F1.opExtrude","SWEPT_EDGE",EDGE,{"disambiguationData":[OSD([sQuery(id+"F0.wireOp",EDGE,"E103.bottom"),sQuery(id+"F0.wireOp",EDGE,"E103.left")])]});
            fillet(context, id + "F4", {"entities" : qUnion([Q0, Q1, Q2, Q3, Q4, Q5, Q6, Q7, Q8]), "radius" : 19.05 * mm, "tangentPropagation" : true, "allowEdgeOverflow" : false});
        }
        {
            var Q0;
            Q0=makeQuery(id+"F0.imprint","IMPRINT",FACE,{"disambiguationData":[TD([[makeQuery(id+"F0.imprint","IMPRINT",EDGE,{"derivedFrom":sQuery(id+"F0.wireOp",EDGE,"E91")}),1.0]])]});
            extrude(context, id + "F5", {"entities" : qUnion([Q0]), "depth" : 133.86 * mm});
        }
        {
            var Q0;
            Q0=makeQuery(id+"F1.opExtrude","SWEPT_FACE",FACE,{"disambiguationData":[OSD([sQuery(id+"F0.wireOp",EDGE,"E103.top")])]});
            var sketch = newSketch(context, id + "F6", { "sketchPlane" : qUnion([Q0])});
            skCircle(sketch, "E169", {"center": v(1098.7, 9.4) * mm, "radius": 3.18 * mm});
            skPoint(sketch, "E169.centerSnap0", {"position": v(1079.65, 9.4) * mm});
            skSolve(sketch);
        }
        {
            var Q0;
            Q0=makeQuery(id+"F6.imprint","IMPRINT",FACE,{"disambiguationData":[TD([[makeQuery(id+"F6.imprint","IMPRINT",EDGE,{"derivedFrom":sQuery(id+"F6.wireOp",EDGE,"E169")}),1.0]])]});
            extrude(context, id + "F7", {"entities" : qUnion([Q0]), "operationType" : NewBodyOperationType.REMOVE, "oppositeDirection" : true, "depth" : 22.22 * mm});
        }
    });
